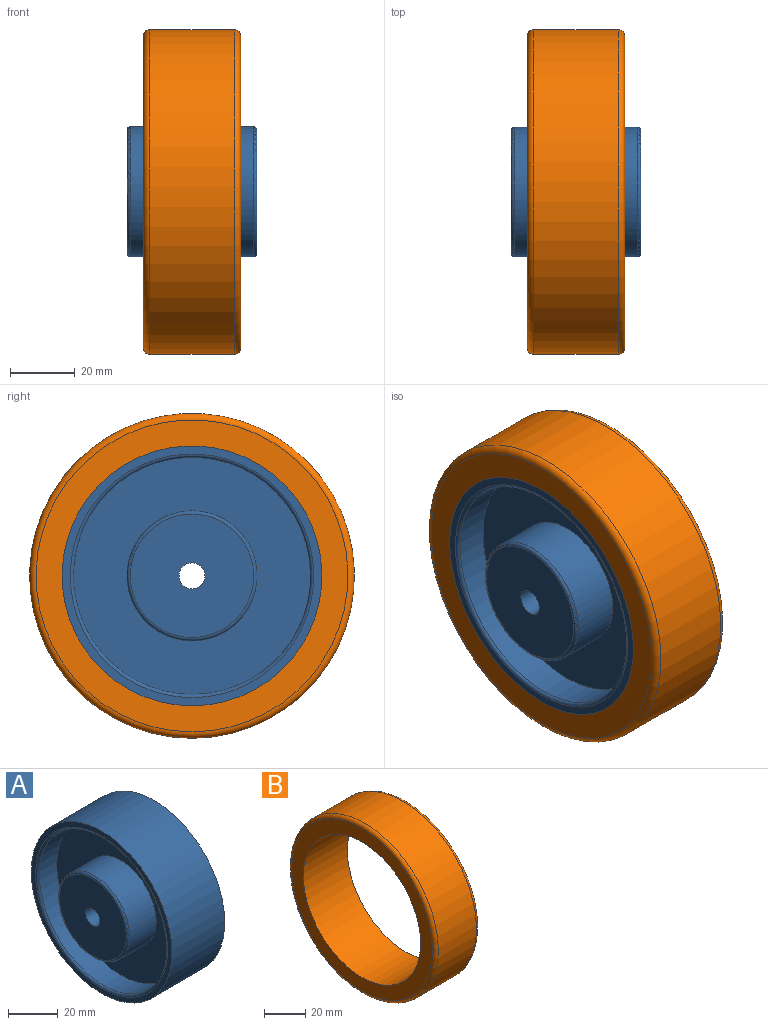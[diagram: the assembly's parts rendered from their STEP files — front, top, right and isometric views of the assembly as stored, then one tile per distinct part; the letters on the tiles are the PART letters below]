
ASSEMBLY  parts=2 mates=1
PART A: 16 faces, bbox 40x82.7x82.7 mm
  f0: cylinder r=40mm len=80mm, axis (-1,0,0), area 7539.8mm2, adj f1,f2
  f1: plane 80x80mm, normal (1,0,0), area 608.7mm2, adj f0,f14
  f2: plane 80x80mm, normal (-1,0,0), area 608.7mm2, adj f0,f11
  f3: cylinder r=36.5mm len=73mm, axis (-1,0,0), area 2293.4mm2, adj f4,f11
  f4: plane 73x73mm, normal (-1,0,0), area 2928.7mm2, adj f3,f9
  f5: cylinder r=36.5mm len=73mm, axis (1,0,0), area 2293.4mm2, adj f6,f14
  f6: plane 73x73mm, normal (1,0,0), area 2928.7mm2, adj f5,f8
  f7: plane 38x38mm, normal (1,0,0), area 1083.8mm2, adj f12,f15
  f8: cylinder r=20mm len=40mm, axis (1,0,0), area 1885mm2, adj f6,f12
  f9: cylinder r=20mm len=40mm, axis (1,0,0), area 1885mm2, adj f4,f13
  f10: plane 38x38mm, normal (-1,0,0), area 1083.8mm2, adj f13,f15
  f11: torus R=37.5mm, axis (1,0,0), area 363.8mm2, adj f2,f3
  f12: torus R=19mm, axis (-1,0,0), area 193.8mm2, adj f7,f8
  f13: torus R=19mm, axis (-1,0,0), area 193.8mm2, adj f9,f10
  f14: torus R=37.5mm, axis (1,0,0), area 363.8mm2, adj f1,f5
  f15: cylinder r=4mm len=40mm, axis (-1,0,0), area 1005.3mm2, adj f7,f10
PART B: 6 faces, bbox 30x108.2x108.2 mm
  f0: cylinder r=40mm len=80mm, axis (-1,0,0), area 7539.8mm2, adj f2,f3
  f1: cylinder r=50mm len=100mm, axis (-1,0,0), area 8168.1mm2, adj f4,f5
  f2: plane 96x96mm, normal (-1,0,0), area 2211.7mm2, adj f0,f5
  f3: plane 96x96mm, normal (1,0,0), area 2211.7mm2, adj f0,f4
  f4: torus R=48mm, axis (1,0,0), area 972.6mm2, adj f1,f3
  f5: torus R=48mm, axis (1,0,0), area 972.6mm2, adj f1,f2
PLACE A t=(-35.21,-9.89,2.67)mm
PLACE B t=(-35.21,-9.89,2.67)mm
MATE fastened A.f0 <-> B.f1  axis (1,0,0) through (-5.21,-9.89,2.67)mm
